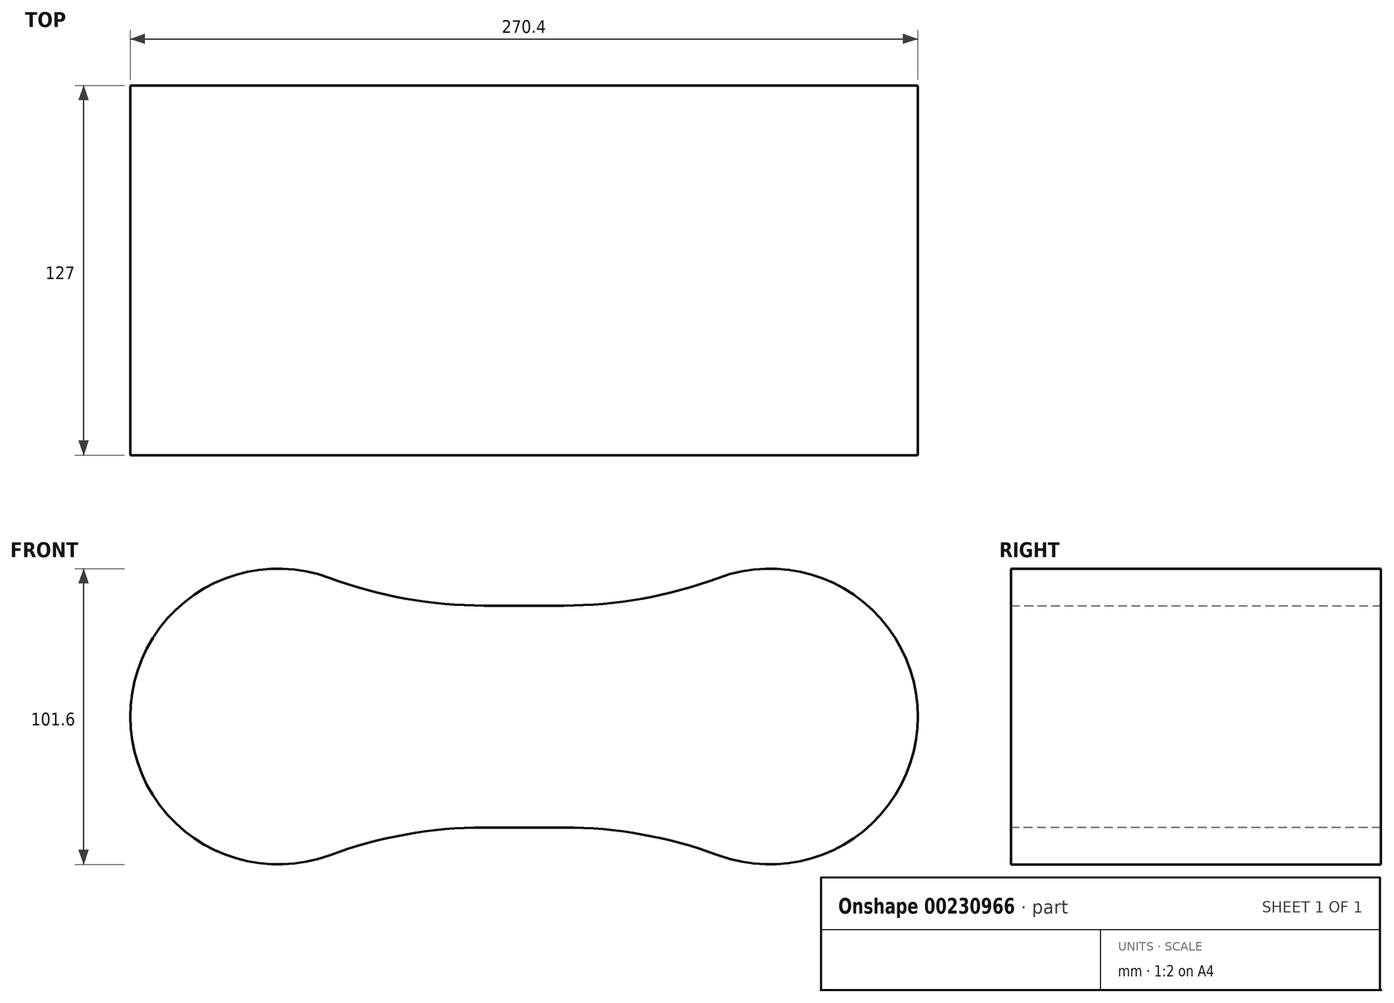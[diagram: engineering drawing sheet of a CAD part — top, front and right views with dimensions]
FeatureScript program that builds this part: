
annotation { "Feature Type Name" : "Feature", "Feature Type Description" : "" }
export const myFeature = defineFeature(function(context is Context, id is Id, definition is map)
    precondition{}
    {
        {
            var Q0;
            Q0=qCreatedBy(makeId("Front.planeOp"),FACE);
            var sketch = newSketch(context, id + "F0", { "sketchPlane" : qUnion([Q0])});
            skCircle(sketch, "E0", {"center": v(-84.4, 0) * mm, "radius": 50.8 * mm});
            skCircle(sketch, "E1", {"center": v(84.4, 0) * mm, "radius": 50.8 * mm});
            skLineSegment(sketch, "E2", {"start": v(-84.4, 0) * mm, "end": v(84.4, 0) * mm, "construction": true});
            skLineSegment(sketch, "E3", {"start": v(-50.8, 38.1) * mm, "end": v(50.8, 38.1) * mm});
            skLineSegment(sketch, "E4", {"start": v(-50.8, -38.1) * mm, "end": v(50.8, -38.1) * mm});
            skSolve(sketch);
        }
        {
            var Q0;
            Q0=qSketchRegion(id+"F0",true);
            extrude(context, id + "F1", {"entities" : qUnion([Q0]), "endBound" : BoundingType.SYMMETRIC, "depth" : 127 * mm});
        }
        {
            var Q0;
            Q0=makeQuery(id+"F1.opExtrude","SWEPT_EDGE",EDGE,{"disambiguationData":[OSD([sQuery(id+"F0.wireOp",EDGE,"E0"),sQuery(id+"F0.wireOp",EDGE,"E3")])]});
            var Q1;
            Q1=makeQuery(id+"F1.opExtrude","SWEPT_EDGE",EDGE,{"disambiguationData":[OSD([sQuery(id+"F0.wireOp",EDGE,"E1"),sQuery(id+"F0.wireOp",EDGE,"E3")])]});
            var Q2;
            Q2=makeQuery(id+"F1.opExtrude","SWEPT_EDGE",EDGE,{"disambiguationData":[OSD([sQuery(id+"F0.wireOp",EDGE,"E0"),sQuery(id+"F0.wireOp",EDGE,"E4")])]});
            var Q3;
            Q3=makeQuery(id+"F1.opExtrude","SWEPT_EDGE",EDGE,{"disambiguationData":[OSD([sQuery(id+"F0.wireOp",EDGE,"E1"),sQuery(id+"F0.wireOp",EDGE,"E4")])]});
            fillet(context, id + "F2", {"entities" : qUnion([Q0, Q1, Q2, Q3]), "radius" : 152.4 * mm, "tangentPropagation" : true, "allowEdgeOverflow" : false});
        }
    });
